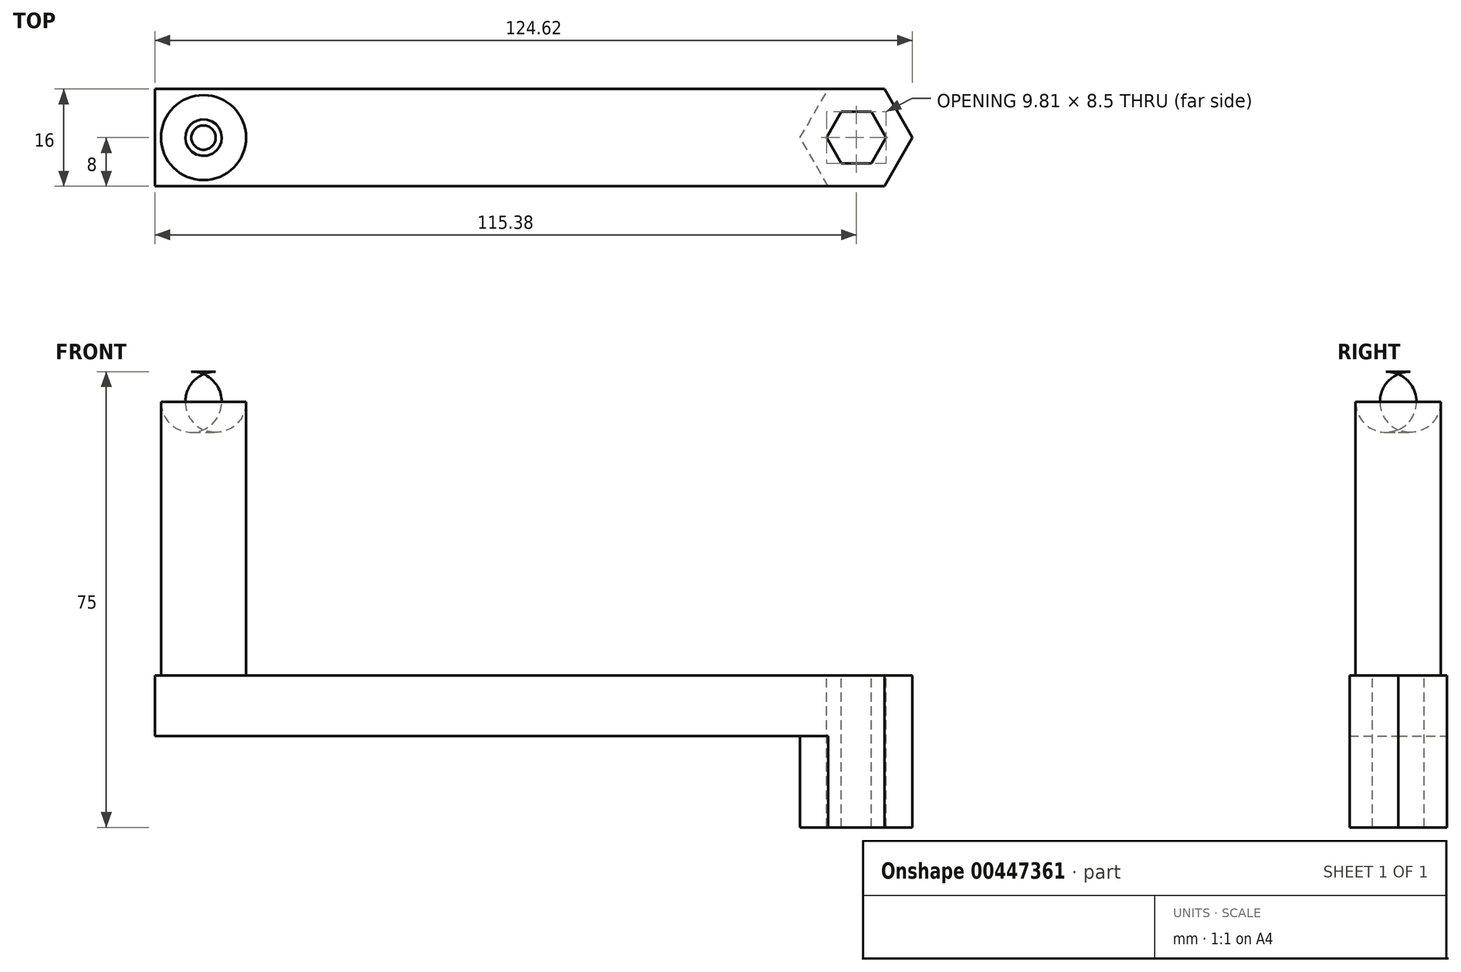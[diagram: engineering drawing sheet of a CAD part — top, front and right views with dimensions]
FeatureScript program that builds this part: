
annotation { "Feature Type Name" : "Feature", "Feature Type Description" : "" }
export const myFeature = defineFeature(function(context is Context, id is Id, definition is map)
    precondition{}
    {
        {
            var Q0;
            Q0=qCreatedBy(makeId("Top.planeOp"),FACE);
            var sketch = newSketch(context, id + "F0", { "sketchPlane" : qUnion([Q0])});
            skCircle(sketch, "E0.cCircle", {"center": v(0, 0) * mm, "radius": 4.25 * mm, "construction": true});
            skLineSegment(sketch, "E0.0", {"start": v(4.9, 0) * mm, "end": v(2.45, -4.25) * mm});
            skLineSegment(sketch, "E0.1", {"start": v(2.45, -4.25) * mm, "end": v(-2.45, -4.25) * mm});
            skLineSegment(sketch, "E0.2", {"start": v(-2.45, -4.25) * mm, "end": v(-4.9, 0) * mm});
            skLineSegment(sketch, "E0.3", {"start": v(-4.9, 0) * mm, "end": v(-2.45, 4.25) * mm});
            skLineSegment(sketch, "E0.4", {"start": v(-2.45, 4.25) * mm, "end": v(2.45, 4.25) * mm});
            skLineSegment(sketch, "E0.5", {"start": v(2.45, 4.25) * mm, "end": v(4.9, 0) * mm});
            skPoint(sketch, "E0.0.midPoint", {"position": v(3.68, -2.13) * mm});
            skCircle(sketch, "E1.cCircle", {"center": v(0, 0) * mm, "radius": 8 * mm, "construction": true});
            skLineSegment(sketch, "E1.0", {"start": v(9.24, 0) * mm, "end": v(4.62, -8) * mm});
            skLineSegment(sketch, "E1.1", {"start": v(4.62, -8) * mm, "end": v(-4.62, -8) * mm});
            skLineSegment(sketch, "E1.2", {"start": v(-4.62, -8) * mm, "end": v(-9.24, 0) * mm});
            skLineSegment(sketch, "E1.3", {"start": v(-9.24, 0) * mm, "end": v(-4.62, 8) * mm});
            skLineSegment(sketch, "E1.4", {"start": v(-4.62, 8) * mm, "end": v(4.62, 8) * mm});
            skLineSegment(sketch, "E1.5", {"start": v(4.62, 8) * mm, "end": v(9.24, 0) * mm});
            skPoint(sketch, "E1.0.midPoint", {"position": v(6.93, -4) * mm});
            skLineSegment(sketch, "E2", {"start": v(-4.62, 8) * mm, "end": v(-115.38, 8) * mm});
            skLineSegment(sketch, "E3", {"start": v(-115.38, 8) * mm, "end": v(-115.38, -8) * mm});
            skLineSegment(sketch, "E4", {"start": v(-115.38, -8) * mm, "end": v(-4.62, -8) * mm});
            skSolve(sketch);
        }
        {
            var Q0;
            Q0=makeQuery(id+"F0.imprint","IMPRINT",FACE,{"disambiguationData":[TD([[makeQuery(id+"F0.imprint","IMPRINT",EDGE,{"derivedFrom":sQuery(id+"F0.wireOp",EDGE,"E1.2")}),1.0]])]});
            extrude(context, id + "F1", {"entities" : qUnion([Q0]), "oppositeDirection" : true, "depth" : 10 * mm});
        }
        {
            var Q0;
            Q0=makeQuery(id+"F0.imprint","IMPRINT",FACE,{"disambiguationData":[TD([[makeQuery(id+"F0.imprint","IMPRINT",EDGE,{"derivedFrom":sQuery(id+"F0.wireOp",EDGE,"E0.0")}),1.0]])]});
            extrude(context, id + "F2", {"entities" : qUnion([Q0]), "operationType" : NewBodyOperationType.ADD, "oppositeDirection" : true, "depth" : 25 * mm});
        }
        {
            var Q0;
            Q0=makeQuery(id+"F1.opExtrude","CAP_FACE",FACE,{"disambiguationData":[OSD([sQuery(id+"F0.wireOp",EDGE,"E1.2"),sQuery(id+"F0.wireOp",EDGE,"E1.3"),sQuery(id+"F0.wireOp",EDGE,"E2"),sQuery(id+"F0.wireOp",EDGE,"E3"),sQuery(id+"F0.wireOp",EDGE,"E4")])],"isStart":false});
            var sketch = newSketch(context, id + "F3", { "sketchPlane" : qUnion([Q0])});
            skCircle(sketch, "E5", {"center": v(-107.38, 0) * mm, "radius": 7 * mm});
            skSolve(sketch);
        }
        {
            var Q0;
            Q0=makeQuery(id+"F3.imprint","IMPRINT",FACE,{"disambiguationData":[TD([[makeQuery(id+"F3.imprint","IMPRINT",EDGE,{"derivedFrom":sQuery(id+"F3.wireOp",EDGE,"E5")}),1.0]])]});
            extrude(context, id + "F4", {"entities" : qUnion([Q0]), "operationType" : NewBodyOperationType.ADD, "oppositeDirection" : true, "depth" : 60 * mm});
        }
        {
            var Q0;
            Q0=makeQuery(id+"F4.opExtrude","CAP_FACE",FACE,{"disambiguationData":[OSD([sQuery(id+"F3.wireOp",EDGE,"E5")])],"isStart":false});
            fillet(context, id + "F5", {"entities" : qUnion([Q0]), "radius" : 5 * mm, "tangentPropagation" : true, "allowEdgeOverflow" : false});
        }
    });
